# Revit family: P2WK-P.BIM
name_source: partatom
category: Fire Alarm Devices
units: mm (PartAtom-declared; Revit-internal decimal feet)

## family parameters
Cut with Voids When Loaded = No
Host = Face
Maintain Annotation Orientation = Yes
OmniClass Number = 23.85.30.21
OmniClass Title = Environmental Detection/Registration
Part Type = Normal
Room Calculation Point = No
Round Connector Dimension = Use Diameter
Shared = No

## types (11) — shared parameters
Backbox = Fire_Alarm-AV-Backbox-Wall-System_Sensor : Red
Default Elevation = 6' - 8"
Electrical Connector = NAC
Height = 0' - 2 1/2"
Label Insert = Fire_HS : FIRE White
Length = 0' - 5 19/32"
Manufacturer = System Sensor
Mounting Requirements = 4 inch square x 2 1/2" deep electrical box.
Strobe Finish = Plastic-System Sensor-Clear
URL = www.systemsensor.com
Width = 0' - 4 11/16"

## per-type parameters (varying)
| type | Description | Finish | Fire Label | Label Finish | Model | NAC Type |
| 2-Wire_Standard Candela_White | 2 Wire Horn Strobe-Wall Mount-Standard Candela-White | Plastic-System Sensor-White | Yes | Plastic-System Sensor-Red | P2WK |  |
| 2-Wire_Standard Candela_Red | 2 Wire Horn Strobe-Wall Mount-Standard Candela-Red | Plastic-System Sensor-Red | Yes | Plastic-System Sensor-White | P2RK |  |
| 2-Wire_Standard Candela_Red_Plain | 2 Wire Horn Strobe-Wall Mount-Standard Candela-Red-Plain | Plastic-System Sensor-Red | No | Plastic-System Sensor-White | P2RK |  |
| 2-Wire_High Candela_Red | 2 Wire Horn Strobe-Wall Mount-High Candela-Red | Plastic-System Sensor-Red | Yes | Plastic-System Sensor-White | P2RHK | HC |
| 2-Wire_High Candela_Red_Plain | 2 Wire Horn Strobe-Wall Mount-High Candela-Red-Plain | Plastic-System Sensor-Red | No | Plastic-System Sensor-White | P2RHK | HC |
| 2-Wire_Standard Candela_White_Plain | 2 Wire Horn Strobe-Wall Mount-Standard Candela-White-Plain | Plastic-System Sensor-White | No | Plastic-System Sensor-Red | P2WK |  |
| 2-Wire_High Candela_White_Plain | 2 Wire Horn Strobe-Wall Mount-High Candela-White-Plain | Plastic-System Sensor-White | No | Plastic-System Sensor-Red | P2WHK | HC |
| 2-Wire_High Candela_White | 2 Wire Horn Strobe-Wall Mount-High Candela-White | Plastic-System Sensor-White | Yes | Plastic-System Sensor-Red | P2WHK | HC |
| 4-Wire_Standard Candela_Red | 4 Wire Horn Strobe-Wall Mount-Standard Candela-Red | Plastic-System Sensor-Red | Yes | Plastic-System Sensor-White | P4RK |  |
| 4-Wire_Standard Candela_Red_Plain | 4 Wire Horn Strobe-Wall Mount-Standard Candela-Red-Plain | Plastic-System Sensor-Red | No | Plastic-System Sensor-White | P4RK |  |
| 4-Wire_Standard Candela_White | 4 Wire Horn Strobe-Wall Mount-Standard Candela-White | Plastic-System Sensor-White | Yes | Plastic-System Sensor-Red | P4WK |  |

## geometry (parser evidence)
native form markers: Blend x26, Sweep x16
no freeform markers — native parametric forms only
